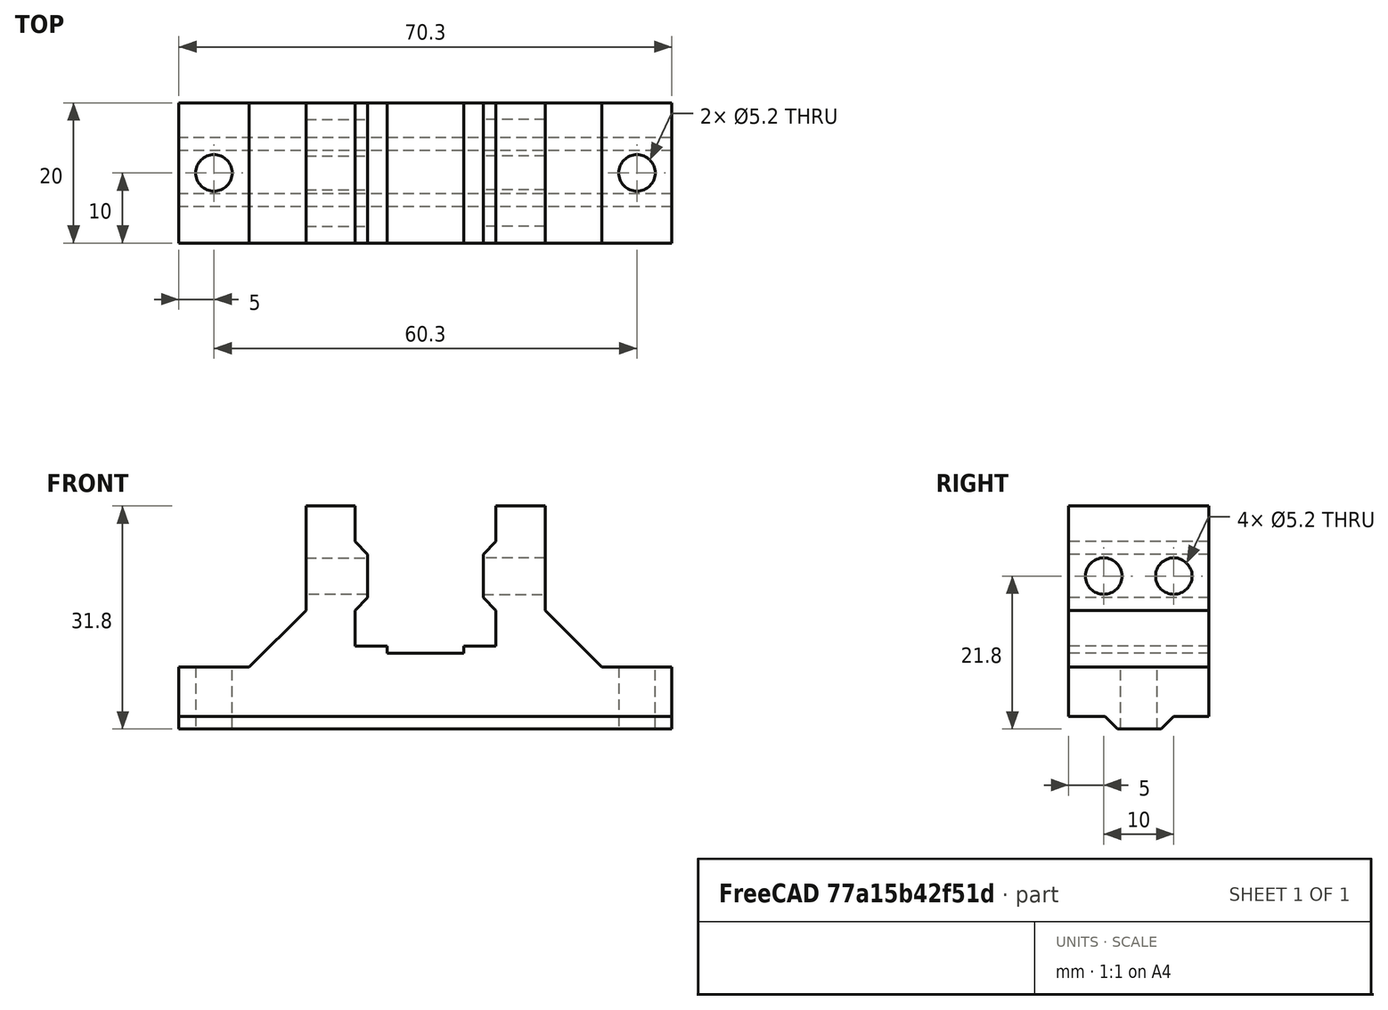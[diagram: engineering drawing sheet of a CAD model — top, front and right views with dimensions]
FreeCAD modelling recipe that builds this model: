
FCSTD DOCUMENT  (FreeCAD 1.0R39109 (Git))
Label: plotter_brace
License: All rights reserved
LicenseURL: https://en.wikipedia.org/wiki/All_rights_reserved
objects: Sketcher::SketchObject×7, PartDesign::Pocket×4, PartDesign::Pad×2, PartDesign::LinearPattern×2, Mesh::Feature×1, PartDesign::Body×1
note: 37 computed .brp shape members not serialized (recipe doc carries the construction recipe); baked Part::Feature solids carry a one-line shape summary decoded from their .brp

FEATURE [Mesh::Feature] _0x20_v_slot  label="20x20_v-slot"
FEATURE [Sketcher::SketchObject] Sketch
  ArcFitTolerance = 1e-06
  AttachmentSupport = -> [XZ_Plane]
  FullyConstrained = false
  MakeInternals = false
  MapMode = 5
  Placement = pos=(0,0,0) rot=(1,0,0;1.5708rad)
  sketch-geometry (26):
    g0: LineSegment StartX=-10.05 StartY=9.99999 StartZ=0 EndX=-10.05 EndY=4.89999 EndZ=0
    g1: LineSegment StartX=-10.05 StartY=4.89999 StartZ=0 EndX=-8.25 EndY=3.10001 EndZ=0
    g2: LineSegment StartX=-8.25 StartY=3.10001 StartZ=0 EndX=-8.25 EndY=-3.09999 EndZ=0
    g3: LineSegment StartX=-8.25 StartY=-3.09999 StartZ=0 EndX=-10.05 EndY=-4.90001 EndZ=0
    g4: LineSegment StartX=-10.05 StartY=-4.90001 StartZ=0 EndX=-10.05 EndY=-10 EndZ=0
    g5: LineSegment StartX=-10.05 StartY=-10 StartZ=0 EndX=-5.47893 EndY=-10 EndZ=0
    g6: LineSegment StartX=-5.47893 StartY=-10 StartZ=0 EndX=-5.47893 EndY=-11 EndZ=0
    g7: LineSegment StartX=-5.47893 StartY=-11 StartZ=0 EndX=5.47893 EndY=-11 EndZ=0
    g8: LineSegment StartX=5.47893 StartY=-11 StartZ=0 EndX=5.47893 EndY=-10 EndZ=0
    g9: LineSegment StartX=5.47893 StartY=-10 StartZ=0 EndX=10.05 EndY=-10 EndZ=0
    g10: LineSegment StartX=10.05 StartY=-10 StartZ=0 EndX=10.05 EndY=-4.90001 EndZ=0
    g11: LineSegment StartX=10.05 StartY=-4.90001 StartZ=0 EndX=8.25 EndY=-3.10001 EndZ=0
    g12: LineSegment StartX=8.25 StartY=-3.10001 StartZ=0 EndX=8.25 EndY=3.09999 EndZ=0
    g13: LineSegment StartX=8.25 StartY=3.09999 StartZ=0 EndX=10.05 EndY=4.89999 EndZ=0
    g14: LineSegment StartX=10.05 StartY=4.89999 StartZ=0 EndX=10.05 EndY=9.99999 EndZ=0
    g15: LineSegment StartX=10.05 StartY=9.99999 StartZ=0 EndX=17.05 EndY=9.99999 EndZ=0
    g16: LineSegment StartX=17.05 StartY=9.99999 StartZ=0 EndX=17.05 EndY=-4.90001 EndZ=0
    g17: LineSegment StartX=17.05 StartY=-4.90001 StartZ=0 EndX=25.15 EndY=-13 EndZ=0
    g18: LineSegment StartX=25.15 StartY=-13 StartZ=0 EndX=35.15 EndY=-13 EndZ=0
    g19: LineSegment StartX=35.15 StartY=-13 StartZ=0 EndX=35.15 EndY=-20 EndZ=0
    g20: LineSegment StartX=35.15 StartY=-20 StartZ=0 EndX=-35.15 EndY=-20 EndZ=0
    g21: LineSegment StartX=-35.15 StartY=-20 StartZ=0 EndX=-35.15 EndY=-13 EndZ=0
    g22: LineSegment StartX=-35.15 StartY=-13 StartZ=0 EndX=-25.15 EndY=-13 EndZ=0
    g23: LineSegment StartX=-25.15 StartY=-13 StartZ=0 EndX=-17.05 EndY=-4.90001 EndZ=0
    g24: LineSegment StartX=-17.05 StartY=-4.90001 StartZ=0 EndX=-17.05 EndY=9.99999 EndZ=0
    g25: LineSegment StartX=-17.05 StartY=9.99999 StartZ=0 EndX=-10.05 EndY=9.99999 EndZ=0
  constraints (75):
    c: Vertical(g0)
    c: Coincident(g0,g1)
    c: Coincident(g1,g2)
    c: Vertical(g2)
    c: Coincident(g2,g3)
    c: Coincident(g3,g4)
    c: Vertical(g4)
    c: Coincident(g4,g5)
    c: Horizontal(g5)
    c: Coincident(g5,g6)
    c: Vertical(g6)
    c: Coincident(g6,g7)
    c: Horizontal(g7)
    c: Coincident(g7,g8)
    c: Vertical(g8)
    c: Coincident(g8,g9)
    c: Horizontal(g9)
    c: Coincident(g9,g10)
    c: Vertical(g10)
    c: Coincident(g10,g11)
    c: Coincident(g11,g12)
    c: Vertical(g12)
    c: Coincident(g12,g13)
    c: Coincident(g13,g14)
    c: Vertical(g14)
    c: Coincident(g14,g15)
    c: Horizontal(g15)
    c: Coincident(g15,g16)
    c: Vertical(g16)
    c: Coincident(g16,g17)
    c: Coincident(g17,g18)
    c: Horizontal(g18)
    c: Coincident(g18,g19)
    c: Vertical(g19)
    c: Coincident(g19,g20)
    c: Coincident(g20,g21)
    c: Vertical(g21)
    c: Coincident(g21,g22)
    c: Horizontal(g22)
    c: Coincident(g22,g23)
    c: Coincident(g23,g24)
    c: Vertical(g24)
    c: Coincident(g24,g25)
    c: Coincident(g25,g0)
    c: Equal(g16,g24)
    c: Parallel(g25,g15)
    c: Equal(g25,g15)
    c: Equal(g14,g0)
    c: Equal(g12,g2)
    c: Equal(g4,g10)
    c: Equal(g9,g5)
    c: Equal(g6,g8)
    c: DistanceY(g8,g8) = 1
    c: DistanceY(g19,g19) = 7
    c: Equal(g21,g19)
    c: Equal(g22,g18)
    c: Symmetric(g19,g20,g-2)
    c: DistanceX(g4,g9) = 20.1
    c: DistanceX(g0,g14) = 20.1
    c: Perpendicular(g3,g1)
    c: Perpendicular(g11,g13)
    c: DistanceY(g2,g2) = 6.2
    c: DistanceX(g3,g2) = 1.8
    c: DistanceX(g11,g10) = 1.8
    c: DistanceY(g9,g14) = 20
    c: DistanceY(g14,g0) = 0
    c: DistanceX(g18,g18) = 10
    c: DistanceX(g15,g15) = 7
    c: Equal(g10,g14)
    c: Equal(g13,g11)
    c: Equal(g17,g23)
    c: Symmetric(g12,g2,g-1)
    c: DistanceY(g19,g9) = 10
    c: Perpendicular(g17,g23)
    c: DistanceY(g16,g10) = 0
FEATURE [PartDesign::Pad] Pad
  Direction = (0,-1,2e-16)
  Length = 20
  Length2 = 10
  Placement = pos=(0,0,0) rot=(1,0,0;1.5708rad)
  Profile = -> Sketch
  ReferenceAxis = -> Sketch [N_Axis]
  Refine = true
  Suppressed = false
  Type = 0
FEATURE [Sketcher::SketchObject] Sketch001
  ArcFitTolerance = 1e-06
  AttachmentSupport = -> [Pad]
  FullyConstrained = true
  MakeInternals = false
  MapMode = 5
  Placement = pos=(8.25,0,0) rot=(0.707107,0,-0.707107;3.14159rad)
  sketch-geometry (1):
    g0: Circle CenterX=0 CenterY=5 CenterZ=0 NormalX=0 NormalY=0 NormalZ=1 AngleXU=0 Radius=2.6
  constraints (3):
    c: Diameter(g0) = 5.2
    c: PointOnObject(g0,g-2)
    c: DistanceY(g-1,g0) = 5
FEATURE [PartDesign::Pocket] Pocket
  BaseFeature = -> Pad
  Direction = (1,0,2e-16)
  Length = 100
  Length2 = 5
  Placement = pos=(0,0,0) rot=(1,0,0;1.5708rad)
  Profile = -> Sketch001
  ReferenceAxis = -> Sketch001 [N_Axis]
  Refine = true
  Suppressed = false
  Type = 0
FEATURE [PartDesign::LinearPattern] LinearPattern
  BaseFeature = -> Pocket
  Direction = -> Sketch001 [V_Axis]
  Length = 10
  Mode = 0
  Occurrences = 2
  Offset = 10
  Originals = -> [Pocket]
  Placement = pos=(0,0,0) rot=(1,0,0;1.5708rad)
  Refine = true
  Suppressed = false
  TransformMode = 0
FEATURE [PartDesign::Pocket] Pocket001
  BaseFeature = -> LinearPattern
  Direction = (1,0,2e-16)
  Length = 40
  Length2 = 5
  Placement = pos=(0,0,0) rot=(1,0,0;1.5708rad)
  Profile = -> Sketch001
  ReferenceAxis = -> Sketch001 [N_Axis]
  Refine = true
  Reversed = true
  Suppressed = false
  Type = 0
FEATURE [PartDesign::LinearPattern] LinearPattern001
  BaseFeature = -> Pocket001
  Direction = -> Sketch001 [V_Axis]
  Length = 10
  Mode = 0
  Occurrences = 2
  Offset = 10
  Originals = -> [Pocket001]
  Placement = pos=(0,0,0) rot=(1,0,0;1.5708rad)
  Refine = true
  Suppressed = false
  TransformMode = 0
FEATURE [Sketcher::SketchObject] Sketch002
  ArcFitTolerance = 1e-06
  AttachmentSupport = -> [LinearPattern001]
  ExternalGeometry = -> [LinearPattern001]
  FullyConstrained = true
  MakeInternals = false
  MapMode = 5
  Placement = pos=(0,-20,0) rot=(1,0,0;1.5708rad)
  sketch-geometry (4):
    g0: LineSegment StartX=-10.05 StartY=4.89999 StartZ=0 EndX=-10.05 EndY=-4.90001 EndZ=0
    g1: LineSegment StartX=-10.05 StartY=-4.90001 StartZ=0 EndX=-8.25 EndY=-3.09999 EndZ=0
    g2: LineSegment StartX=-8.25 StartY=-3.09999 StartZ=0 EndX=-8.25 EndY=3.10001 EndZ=0
    g3: LineSegment StartX=-8.25 StartY=3.10001 StartZ=0 EndX=-10.05 EndY=4.89999 EndZ=0
  constraints (8):
    c: Coincident(g-3,g0)
    c: Coincident(g0,g-5)
    c: Coincident(g0,g1)
    c: Coincident(g1,g-5)
    c: Coincident(g1,g2)
    c: Coincident(g2,g-4)
    c: Coincident(g2,g3)
    c: Coincident(g3,g0)
FEATURE [Sketcher::SketchObject] Sketch003
  ArcFitTolerance = 1e-06
  AttachmentSupport = -> [LinearPattern001]
  ExternalGeometry = -> [LinearPattern001]
  FullyConstrained = true
  MakeInternals = false
  MapMode = 5
  Placement = pos=(35.15,0,0) rot=(0.707107,0,0.707107;3.14159rad)
  sketch-geometry (5):
    g0: GeomPoint X=-20 Y=10 Z=0
    g1: LineSegment StartX=-20 StartY=14.8 StartZ=0 EndX=-20 EndY=5 EndZ=0
    g2: LineSegment StartX=-20 StartY=5 StartZ=0 EndX=-21.8 EndY=6.8 EndZ=0
    g3: LineSegment StartX=-21.8 StartY=6.8 StartZ=0 EndX=-21.8 EndY=13 EndZ=0
    g4: LineSegment StartX=-21.8 StartY=13 StartZ=0 EndX=-20 EndY=14.8 EndZ=0
  constraints (12):
    c: Symmetric(g-3,g-3,g0)
    c: Coincident(g1,g2)
    c: Coincident(g2,g3)
    c: Coincident(g3,g4)
    c: Coincident(g4,g1)
    c: Equal(g2,g4)
    c: Parallel(g1,g3)
    c: DistanceY(g3,g3) = 6.2
    c: DistanceY(g1,g1) = 9.8
    c: Perpendicular(g4,g2)
    c: PointOnObject(g1,g-3)
    c: Symmetric(g0,g-3,g1)
FEATURE [PartDesign::Pad] Pad001
  BaseFeature = -> LinearPattern001
  Direction = (1,0,-2e-16)
  Length = 70.3
  Length2 = 10
  Placement = pos=(0,0,0) rot=(1,0,0;1.5708rad)
  Profile = -> Sketch003
  ReferenceAxis = -> Sketch003 [N_Axis]
  Refine = true
  Reversed = true
  Suppressed = false
  Type = 0
FEATURE [Sketcher::SketchObject] Sketch004
  ArcFitTolerance = 1e-06
  AttachmentSupport = -> [Pad001]
  ExternalGeometry = -> [Pad001]
  FullyConstrained = true
  MakeInternals = false
  MapMode = 5
  Placement = pos=(0,-5.7e-15,-13) rot=(0,0,1;3.14159rad)
  sketch-geometry (1):
    g0: Circle CenterX=-30.15 CenterY=10 CenterZ=0 NormalX=0 NormalY=0 NormalZ=1 AngleXU=0 Radius=2.6
  constraints (2):
    c: Diameter(g0) = 5.2
    c: Symmetric(g-4,g-3,g0)
FEATURE [PartDesign::Pocket] Pocket002
  BaseFeature = -> Pad001
  Direction = (0,0,-1)
  Length = 10
  Length2 = 5
  Placement = pos=(0,0,0) rot=(1,0,0;1.5708rad)
  Profile = -> Sketch004
  ReferenceAxis = -> Sketch004 [N_Axis]
  Refine = true
  Suppressed = false
  Type = 0
FEATURE [Sketcher::SketchObject] Sketch005
  ArcFitTolerance = 1e-06
  AttachmentSupport = -> [Pocket002]
  ExternalGeometry = -> [Pocket002]
  FullyConstrained = true
  MakeInternals = false
  MapMode = 5
  Placement = pos=(0,-5.7e-15,-13) rot=(0,0,1;3.14159rad)
  sketch-geometry (1):
    g0: Circle CenterX=30.15 CenterY=10 CenterZ=0 NormalX=0 NormalY=0 NormalZ=1 AngleXU=0 Radius=2.6
  constraints (2):
    c: Diameter(g0) = 5.2
    c: Symmetric(g-4,g-3,g0)
FEATURE [PartDesign::Pocket] Pocket003
  BaseFeature = -> Pocket002
  Direction = (0,0,-1)
  Length = 10
  Length2 = 5
  Placement = pos=(0,0,0) rot=(1,0,0;1.5708rad)
  Profile = -> Sketch005
  ReferenceAxis = -> Sketch005 [N_Axis]
  Refine = true
  Suppressed = false
  Type = 0
FEATURE [Sketcher::SketchObject] Sketch006
  ArcFitTolerance = 1e-06
  AttachmentSupport = -> [Pocket003]
  FullyConstrained = true
  MakeInternals = false
  MapMode = 5
  Placement = pos=(0,-4.8e-15,-11) rot=(0,0,1;3.14159rad)
FEATURE [PartDesign::Body] Body  label="main"
  AllowCompound = false
  Group = -> [Sketch,Pad,Sketch001,Pocket,LinearPattern,Pocket001,LinearPattern001,Sketch002,Sketch003,Pad001,Sketch004,Pocket002,Sketch005,Pocket003,Sketch006]
  Origin = -> Origin
  Tip = -> Pocket003
